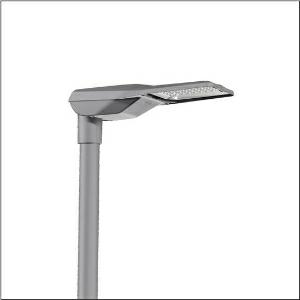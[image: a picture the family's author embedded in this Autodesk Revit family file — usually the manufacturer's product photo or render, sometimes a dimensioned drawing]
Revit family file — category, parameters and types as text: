
# Revit family: streetlight_sl_21_iq_mini___st1_0a_5xe2d31d08jb_a4dc
name_source: partatom
category: Lighting Fixtures
units: mm (PartAtom-declared; Revit-internal decimal feet)

## family parameters
Cut with Voids When Loaded = No
Host = Face
Light Source = No
Part Type = Normal
Room Calculation Point = No
Round Connector Dimension = Use Diameter
Shared = No

## types (1)
- --- (1 x LED, 10820 lm, 71.6 W, 3000K)
    Apparent Load = 72 VA
    CIE Flux Codes = 40 73 97 100 100
    Color Rendering = 70
    Color Temperature = 3000K
    Default Elevation = 1800 mm
    Description = Streetlight SL 21 iQ mini, mast luminaire, primary light control with lens, of PMMA, primary optical cover: cover, of toughened safety glass, transparent, light distribution: ST1.0a, light emission: direct distribution, primary light characteristic: asymmetric, installation type: post-top, side-entry, LED, High Power LED, rated luminous flux: 10.820lm, luminous efficacy: 151lm/W, light colour: 730, colour temperature: 3000K, control gear: iQ-Comfort, control: Auto-Match, Temp-Guard, Lumen-Switch, Night-Set, Smart-Wire, Light-Fading, Desk-Remote (wireless, voltage-free reading and setting of iQ features in the workshop via application-optimized NFC function/RFID function), optimised constant luminous flux control (CLO 2.0), pre-setting: linear dimming characteristic, mains connection: 220..240V, AC, 50/60Hz, start of lifetime: 72W, end of service life: 75W, reduction: 33W, luminaire housing, of diecast aluminium, powder-coated, SITECO metallic grey (DB 702S), corrosivity category C5 high according to DIN EN ISO 12944, please order mast flange separately, inclination adjustable: 0°, 5°, 10°, 15°, sealing non-destructively replaceable, multi-level sealing system, length: 628mm, width: 235mm, height: 110mm, mast flange for spigot size: 42mm (side-entry): 5XC10008XM4, 60/48mm (side-entry/post-top): 5XC10108XM2, 76/60mm (side-entry/post-top): 5XC10108XM1, mounting height: 4..8m, protection rating (complete): IP66, insulation class (complete): insulation class II (safety insulation), certification: CE, ENEC, ENEC+, VDE, impact resistance: IK10, permissible operating ambient temperature for outdoor applications: -40..+50°C, standard-compliant lighting for roads and squares, packaging unit: 1 piece

Light Distribution: ST1.0a
    Height = 110 mm
    Lamp = 1 x LED
    Lamp Light Flux = 10820 lm
    Lamp Power = 71.6 W
    Lamp count = 1
    Length = 625 mm
    Luminous efficacy = 151 lm/W
    Manufacturer = Siteco
    ModVariant = No
    Model = 5XE2D31D08JB
    Number of Poles = 1
    OnlyDefault = Yes
    Power Factor = 1
    Product Name = Streetlight SL 21 iQ mini | ST1.0a
    Product group = mast luminaire | pylon top
    ProductGroupID = 6100
    Protection Class = Protection class II
    Protection Degree = IP 66
    RLX_Detail_Level = 1
    RLX_Emergency_Light_Flux = 0 lm
    RLX_Emergency_Type = 0
    RLX_Emergency_Type_DB = No
    RlxData = <blob elided: 26317 chars, md5=8c6d6e67>
    Socket = socket
    Standby Power = 0 W
    System Light Flux = 10820 lm
    System Power = 72 W
    Type Comments = factory setting: luminous flux: 100 % | dim-lin: 254 | 746 mA
    Type Image = l_1003519.jpg
    URL = http://relux.com
    VarID = @adj_170677
    Voltage = 0 V
    Weight = 0.00 kg
    Width = 234 mm

## geometry (parser evidence)
native form markers: Blend x4, Sweep x10
no freeform markers — native parametric forms only
